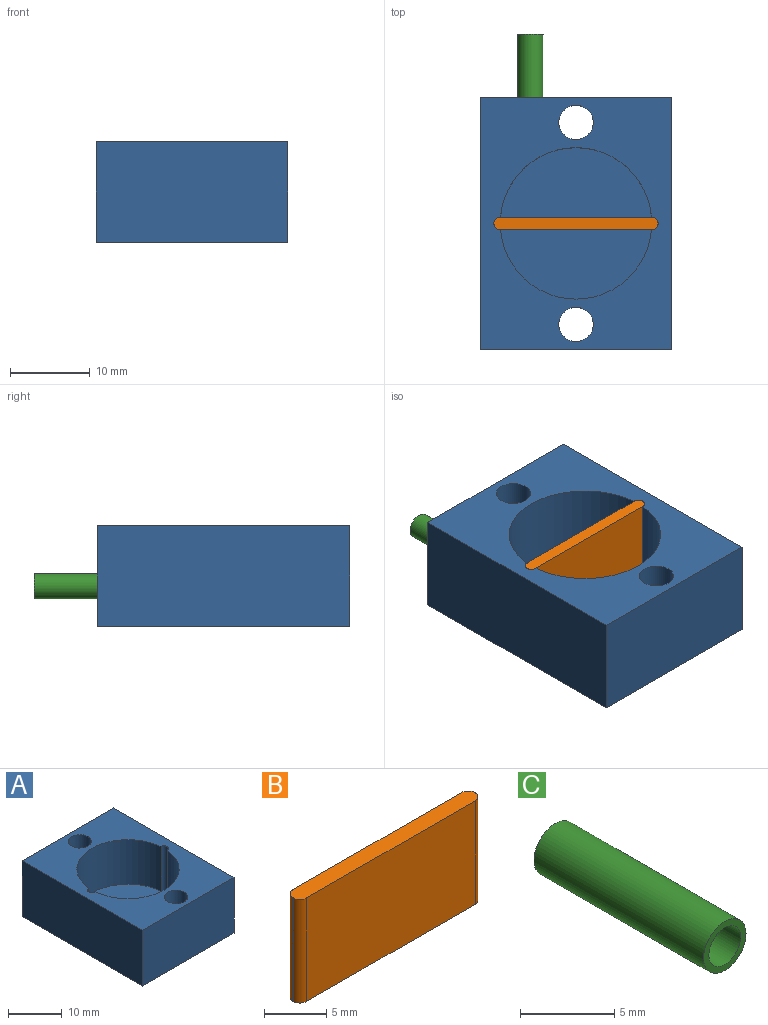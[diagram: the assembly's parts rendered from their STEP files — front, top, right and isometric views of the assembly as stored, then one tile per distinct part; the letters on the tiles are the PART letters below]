
ASSEMBLY  parts=3 mates=2
PART A: 14 faces, bbox 24.1x31.8x12.7 mm
  f0: cylinder r=9.53mm len=18.98mm, axis (0,0,1), area 287.9mm2, adj f7,f10,f11,f12
  f1: plane 31.75x12.7mm, normal (1,0,0), area 403.2mm2, adj f2,f5,f7,f8
  f2: plane 24.13x12.7mm, normal (0,1,0), area 298.5mm2, adj f1,f3,f7,f8,f13
  f3: plane 31.75x12.7mm, normal (-1,0,0), area 403.2mm2, adj f2,f5,f7,f8
  f4: cylinder r=2.16mm len=12.7mm, axis (0,0,-1), area 172.3mm2, adj f7,f8
  f5: plane 24.13x12.7mm, normal (0,-1,0), area 306.5mm2, adj f1,f3,f7,f8
  f6: cylinder r=2.16mm len=12.7mm, axis (0,0,-1), area 172.3mm2, adj f7,f8
  f7: plane 31.75x24.13mm, normal (0,0,1), area 449.8mm2, adj f0,f1,f2,f3,f4,f5,f6,f9
  f8: plane 31.75x24.13mm, normal (0,0,-1), area 736.8mm2, adj f1,f2,f3,f4,f5,f6
  f9: cylinder r=9.53mm len=18.98mm, axis (0,0,1), area 277.8mm2, adj f7,f10,f11,f12,f13
  f10: plane 20.64x19.05mm, normal (0,0,1), area 287mm2, adj f0,f9,f11,f12
  f11: cylinder r=0.79mm len=10.16mm, axis (0,0,1), area 26mm2, adj f0,f7,f9,f10
  f12: cylinder r=0.79mm len=10.16mm, axis (0,0,1), area 26mm2, adj f0,f7,f9,f10
  f13: cylinder r=1.59mm len=9.76mm, axis (0,1,0), area 83.7mm2, adj f2,f9
PART B: 10 faces, bbox 20.6x1.6x10.2 mm
  f0: plane 19.06x10.16mm, normal (0,1,0), area 193.7mm2, adj f1,f3,f7,f9
  f1: plane 20.64x1.59mm, normal (0,0,1), area 32.2mm2, adj f0,f2,f4,f5,f6,f7,f8,f9
  f2: plane 19.06x10.16mm, normal (0,-1,0), area 193.7mm2, adj f1,f3,f6,f8
  f3: plane 20.64x1.59mm, normal (0,0,-1), area 32.2mm2, adj f0,f2,f4,f5,f6,f7,f8,f9
  f4: plane 10.16x0.01mm, normal (1,0,0), area 0.1mm2, adj f1,f3,f8,f9
  f5: plane 10.16x0.01mm, normal (-1,0,0), area 0.1mm2, adj f1,f3,f6,f7
  f6: cylinder r=0.79mm len=10.16mm, axis (0,0,-1), area 12.6mm2, adj f1,f2,f3,f5
  f7: cylinder r=0.79mm len=10.16mm, axis (0,0,1), area 12.6mm2, adj f0,f1,f3,f5
  f8: cylinder r=0.79mm len=10.16mm, axis (0,0,1), area 12.6mm2, adj f1,f2,f3,f4
  f9: cylinder r=0.79mm len=10.16mm, axis (0,0,-1), area 12.6mm2, adj f0,f1,f3,f4
PART C: 4 faces, bbox 3.2x12.7x3.2 mm
  f0: cylinder r=1.19mm len=12.7mm, axis (0,1,0), area 95.3mm2, adj f2,f3
  f1: cylinder r=1.59mm len=12.7mm, axis (0,1,0), area 126.7mm2, adj f2,f3
  f2: plane 3.18x3.18mm, normal (0,-1,0), area 3.4mm2, adj f0,f1
  f3: plane 3.18x3.18mm, normal (0,1,0), area 3.4mm2, adj f0,f1
PLACE A at identity fixed
PLACE B t=(-0.01,-0.01,7.62)mm
PLACE C rot(axis=(0,1,0),180deg) t=(-5.72,23.8,5.08)mm
MATE fastened A.f13 <-> C.f0  axis (0,1,0) through (-5.72,15.88,5.08)mm
MATE fastened B.f9 <-> A.f11  axis (0,0,-1) through (9.52,0,2.54)mm
